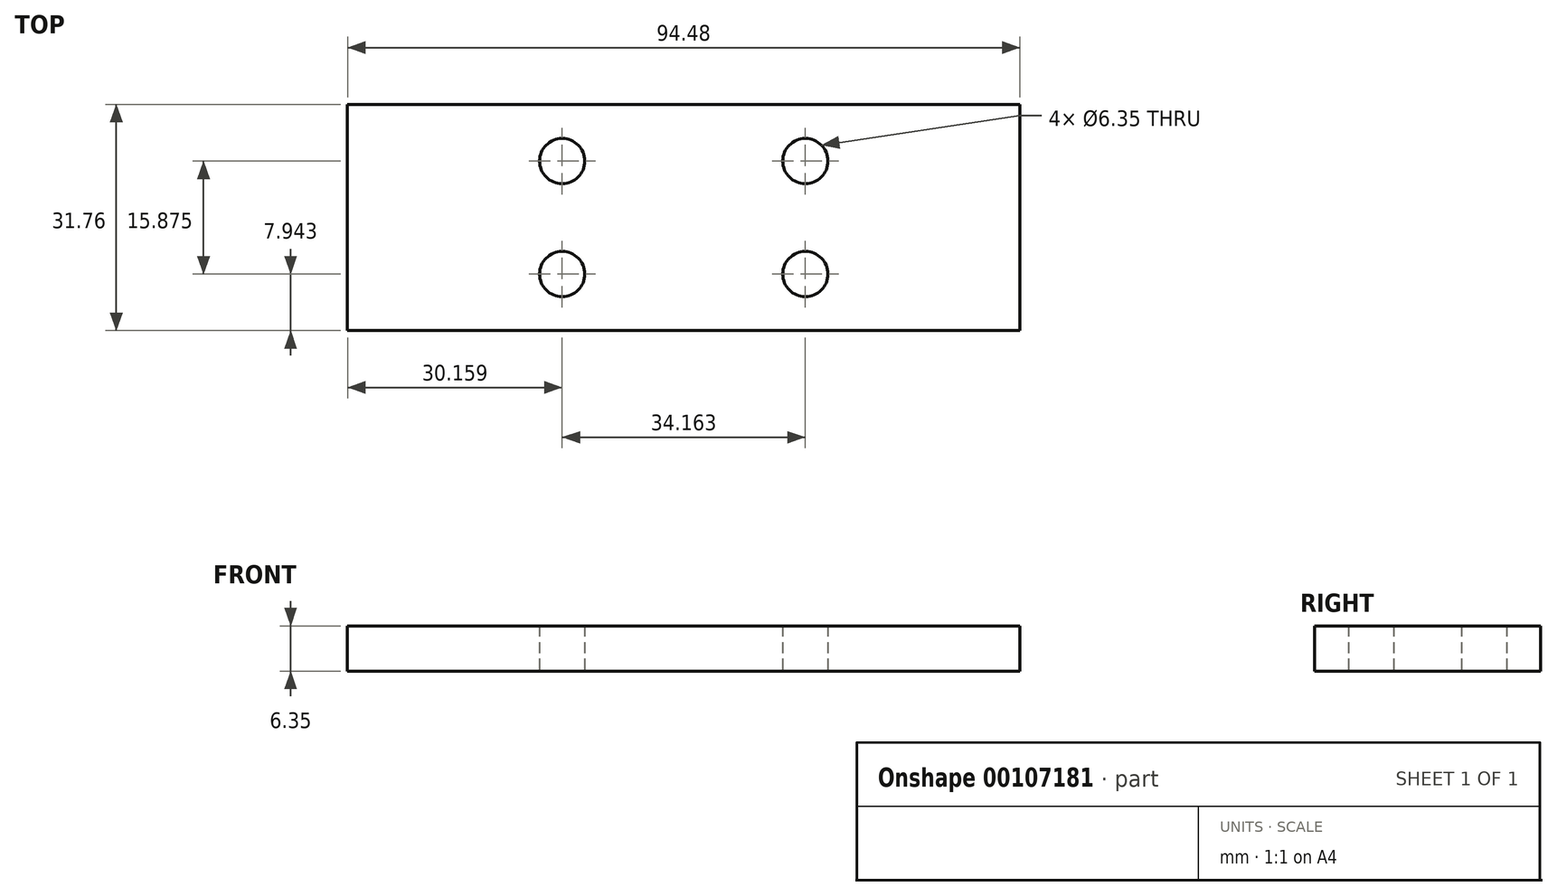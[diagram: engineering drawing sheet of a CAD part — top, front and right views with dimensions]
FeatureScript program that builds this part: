
annotation { "Feature Type Name" : "Feature", "Feature Type Description" : "" }
export const myFeature = defineFeature(function(context is Context, id is Id, definition is map)
    precondition{}
    {
        {
            var Q0;
            Q0=qCreatedBy(makeId("Top.planeOp"),FACE);
            var sketch = newSketch(context, id + "F0", { "sketchPlane" : qUnion([Q0])});
            skLineSegment(sketch, "E0.bottom", {"start": v(-47.24, 15.88) * mm, "end": v(47.24, 15.88) * mm});
            skLineSegment(sketch, "E0.top", {"start": v(-47.24, -15.88) * mm, "end": v(47.24, -15.88) * mm});
            skLineSegment(sketch, "E0.left", {"start": v(-47.24, 15.88) * mm, "end": v(-47.24, -15.88) * mm});
            skLineSegment(sketch, "E0.right", {"start": v(47.24, 15.88) * mm, "end": v(47.24, -15.88) * mm});
            skPoint(sketch, "E0.middle", {"position": v(0, 0) * mm});
            skCircle(sketch, "E1", {"center": v(-17.08, 7.94) * mm, "radius": 3.18 * mm});
            skCircle(sketch, "E2.MirrorC", {"center": v(17.08, 7.94) * mm, "radius": 3.18 * mm});
            skCircle(sketch, "E3.MirrorC", {"center": v(-17.08, -7.94) * mm, "radius": 3.18 * mm});
            skCircle(sketch, "E4.MirrorC", {"center": v(17.08, -7.94) * mm, "radius": 3.18 * mm});
            skSolve(sketch);
        }
        {
            var Q0;
            Q0=makeQuery(id+"F0.imprint","IMPRINT",FACE,{"disambiguationData":[TD([[makeQuery(id+"F0.imprint","IMPRINT",EDGE,{"derivedFrom":sQuery(id+"F0.wireOp",EDGE,"E0.bottom")}),-1.0]])]});
            extrude(context, id + "F1", {"entities" : qUnion([Q0]), "depth" : 6.35 * mm});
        }
    });
